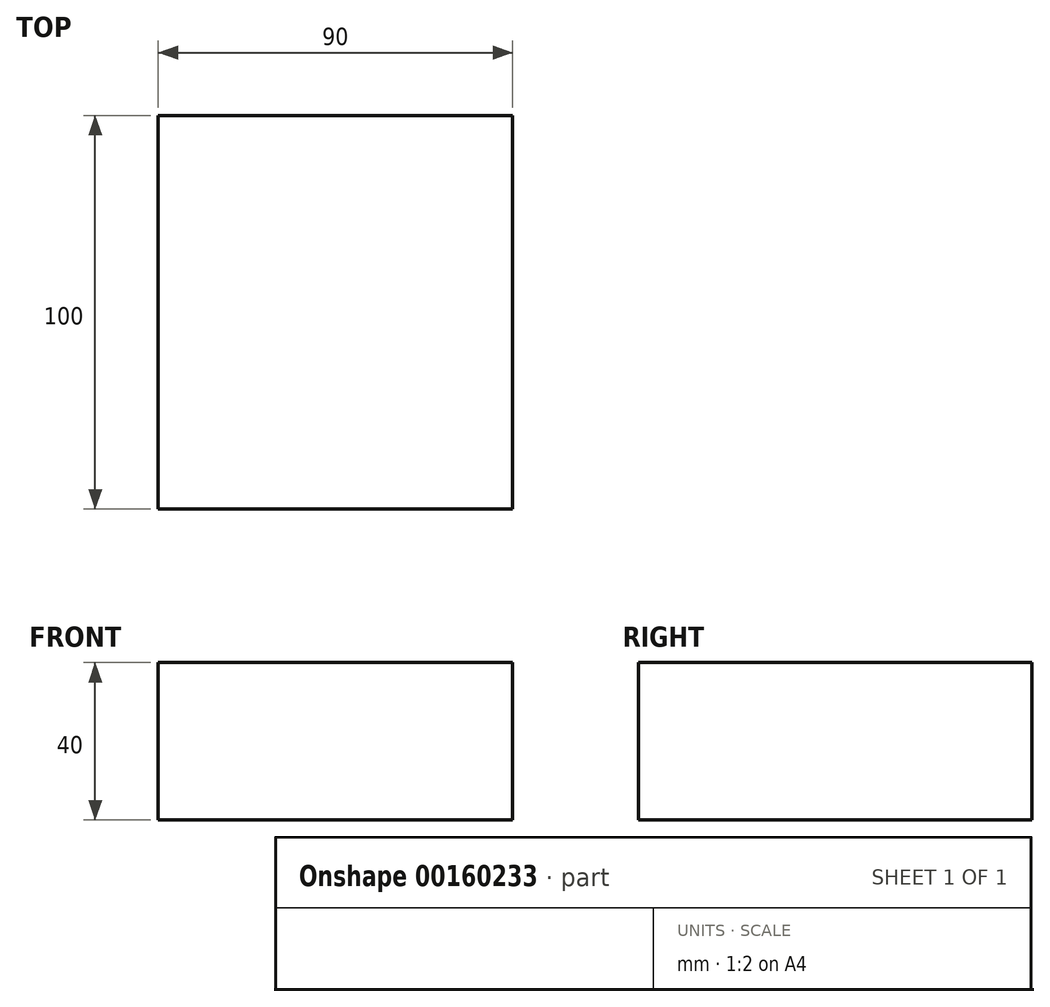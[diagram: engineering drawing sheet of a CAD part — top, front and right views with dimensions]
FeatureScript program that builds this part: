
annotation { "Feature Type Name" : "Feature", "Feature Type Description" : "" }
export const myFeature = defineFeature(function(context is Context, id is Id, definition is map)
    precondition{}
    {
        {
            var Q0;
            Q0=qCreatedBy(makeId("Front.planeOp"),FACE);
            var sketch = newSketch(context, id + "F0", { "sketchPlane" : qUnion([Q0])});
            skLineSegment(sketch, "E0.bottom", {"start": v(45, -20) * mm, "end": v(-45, -20) * mm});
            skLineSegment(sketch, "E0.top", {"start": v(45, 20) * mm, "end": v(-45, 20) * mm});
            skLineSegment(sketch, "E0.left", {"start": v(45, -20) * mm, "end": v(45, 20) * mm});
            skLineSegment(sketch, "E0.right", {"start": v(-45, -20) * mm, "end": v(-45, 20) * mm});
            skPoint(sketch, "E0.middle", {"position": v(0, 0) * mm});
            skSolve(sketch);
        }
        {
            var Q0;
            Q0=makeQuery(id+"F0.imprint","IMPRINT",FACE,{"disambiguationData":[TD([[makeQuery(id+"F0.imprint","IMPRINT",EDGE,{"derivedFrom":sQuery(id+"F0.wireOp",EDGE,"E0.bottom")}),-1.0]])]});
            var Q1;
            Q1 = qSketchRegion(id + "F2", true);
            extrude(context, id + "F1", {"entities" : qUnion([Q0, Q1]), "depth" : 100 * mm});
        }
    });
